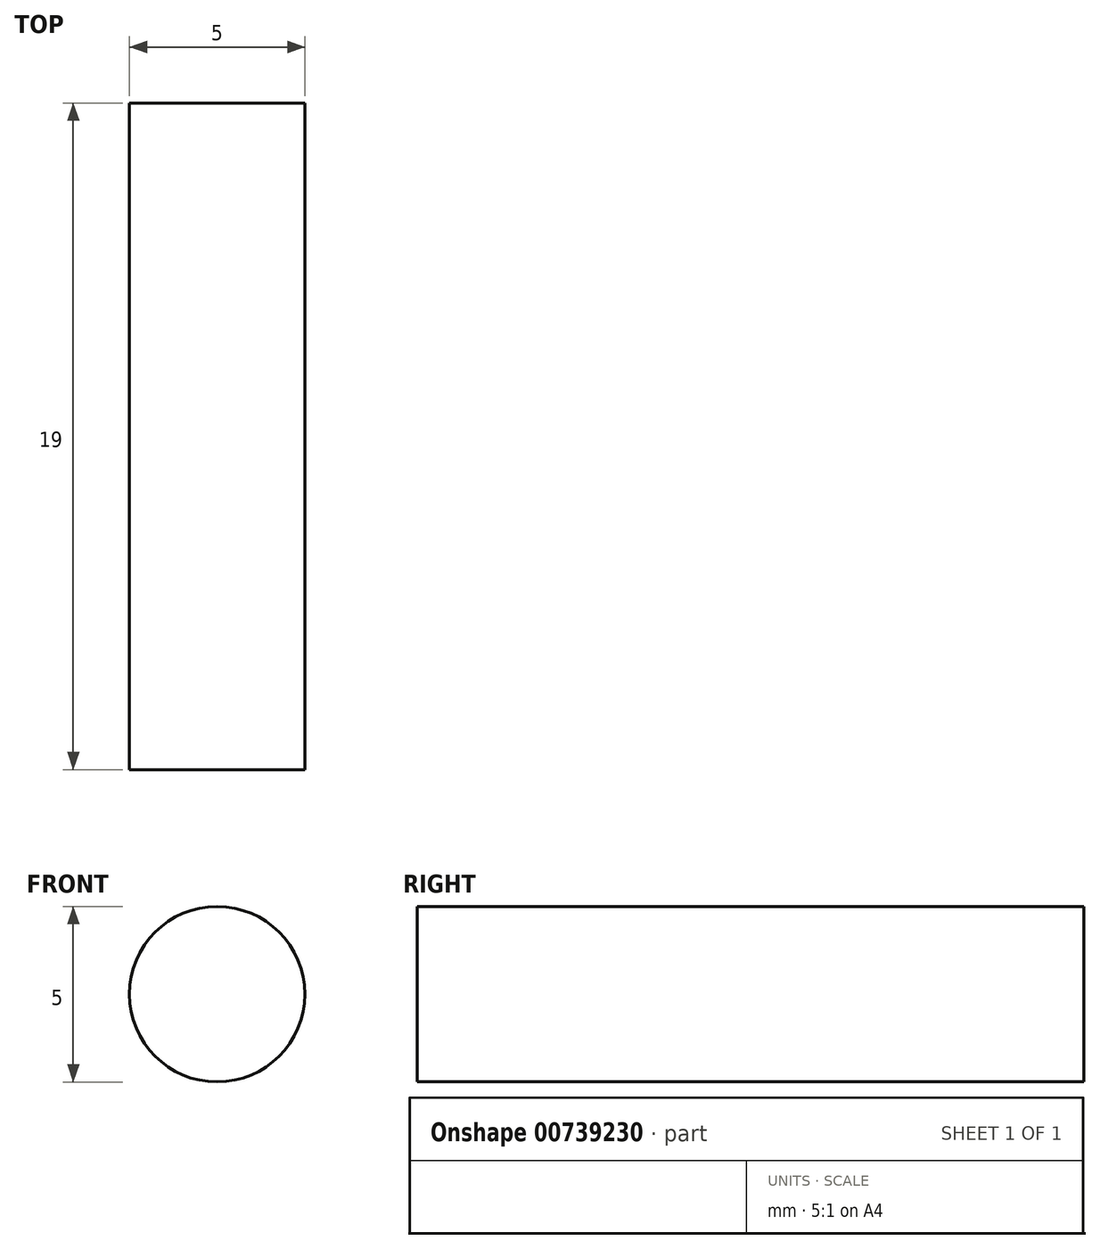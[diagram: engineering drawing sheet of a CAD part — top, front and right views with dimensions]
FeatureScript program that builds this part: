
annotation { "Feature Type Name" : "Feature", "Feature Type Description" : "" }
export const myFeature = defineFeature(function(context is Context, id is Id, definition is map)
    precondition{}
    {
        {
            var Q0;
            Q0=qCreatedBy(makeId("Front.planeOp"),FACE);
            var sketch = newSketch(context, id + "F0", { "sketchPlane" : qUnion([Q0])});
            skCircle(sketch, "E0", {"center": v(-2.63, 1.08) * mm, "radius": 2.5 * mm});
            skSolve(sketch);
        }
        {
            var Q0;
            Q0 = qSketchRegion(id + "F0", true);
            extrude(context, id + "F1", {"entities" : qUnion([Q0]), "depth" : 19 * mm, "offsetDistance" : 25.4 * mm});
        }
    });
